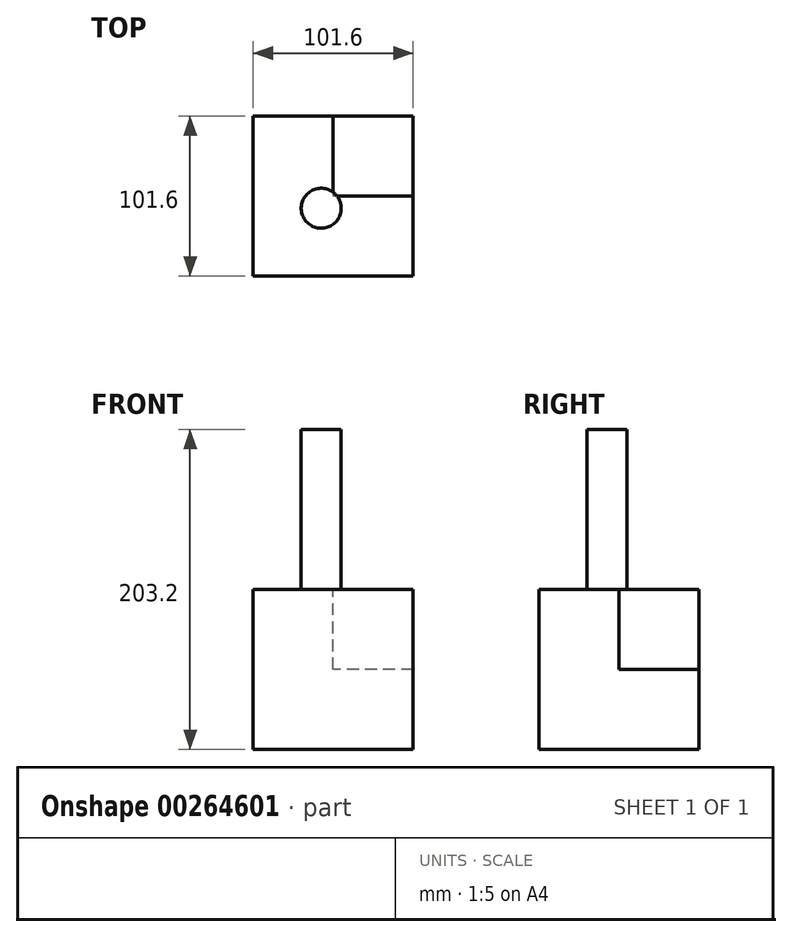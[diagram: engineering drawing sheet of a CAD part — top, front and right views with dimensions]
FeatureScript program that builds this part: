
annotation { "Feature Type Name" : "Feature", "Feature Type Description" : "" }
export const myFeature = defineFeature(function(context is Context, id is Id, definition is map)
    precondition{}
    {
        {
            var Q0;
            Q0=qCreatedBy(makeId("Front.planeOp"),FACE);
            var sketch = newSketch(context, id + "F0", { "sketchPlane" : qUnion([Q0])});
            skLineSegment(sketch, "E0.bottom", {"start": v(0, 0) * mm, "end": v(-101.6, 0) * mm});
            skLineSegment(sketch, "E0.top", {"start": v(0, 101.6) * mm, "end": v(-101.6, 101.6) * mm});
            skLineSegment(sketch, "E0.left", {"start": v(0, 0) * mm, "end": v(0, 101.6) * mm});
            skLineSegment(sketch, "E0.right", {"start": v(-101.6, 0) * mm, "end": v(-101.6, 101.6) * mm});
            skSolve(sketch);
        }
        {
            var Q0;
            Q0 = qSketchRegion(id + "F0", true);
            extrude(context, id + "F1", {"entities" : qUnion([Q0]), "depth" : 101.6 * mm});
        }
        {
            var Q0;
            Q0=makeQuery(id+"F1.opExtrude","SWEPT_FACE",FACE,{"disambiguationData":[OSD([sQuery(id+"F0.wireOp",EDGE,"E0.top")])]});
            var sketch = newSketch(context, id + "F2", { "sketchPlane" : qUnion([Q0])});
            skCircle(sketch, "E1", {"center": v(-58.38, -58.56) * mm, "radius": 12.7 * mm});
            skSolve(sketch);
        }
        {
            var Q0;
            Q0 = qSketchRegion(id + "F2", true);
            extrude(context, id + "F3", {"entities" : qUnion([Q0]), "operationType" : NewBodyOperationType.ADD, "depth" : 101.6 * mm});
        }
        {
            var Q0;
            Q0=makeQuery(id+"F1.opExtrude","SWEPT_FACE",FACE,{"disambiguationData":[OSD([sQuery(id+"F0.wireOp",EDGE,"E0.top")])]});
            var sketch = newSketch(context, id + "F4", { "sketchPlane" : qUnion([Q0])});
            skLineSegment(sketch, "E2.bottom", {"start": v(0, 0) * mm, "end": v(-50.8, 0) * mm});
            skLineSegment(sketch, "E2.top", {"start": v(0, -50.8) * mm, "end": v(-50.8, -50.8) * mm});
            skLineSegment(sketch, "E2.left", {"start": v(0, 0) * mm, "end": v(0, -50.8) * mm});
            skLineSegment(sketch, "E2.right", {"start": v(-50.8, 0) * mm, "end": v(-50.8, -50.8) * mm});
            skSolve(sketch);
        }
        {
            var Q0;
            Q0 = qSketchRegion(id + "F4", true);
            extrude(context, id + "F5", {"entities" : qUnion([Q0]), "operationType" : NewBodyOperationType.REMOVE, "oppositeDirection" : true, "depth" : 50.8 * mm});
        }
    });
